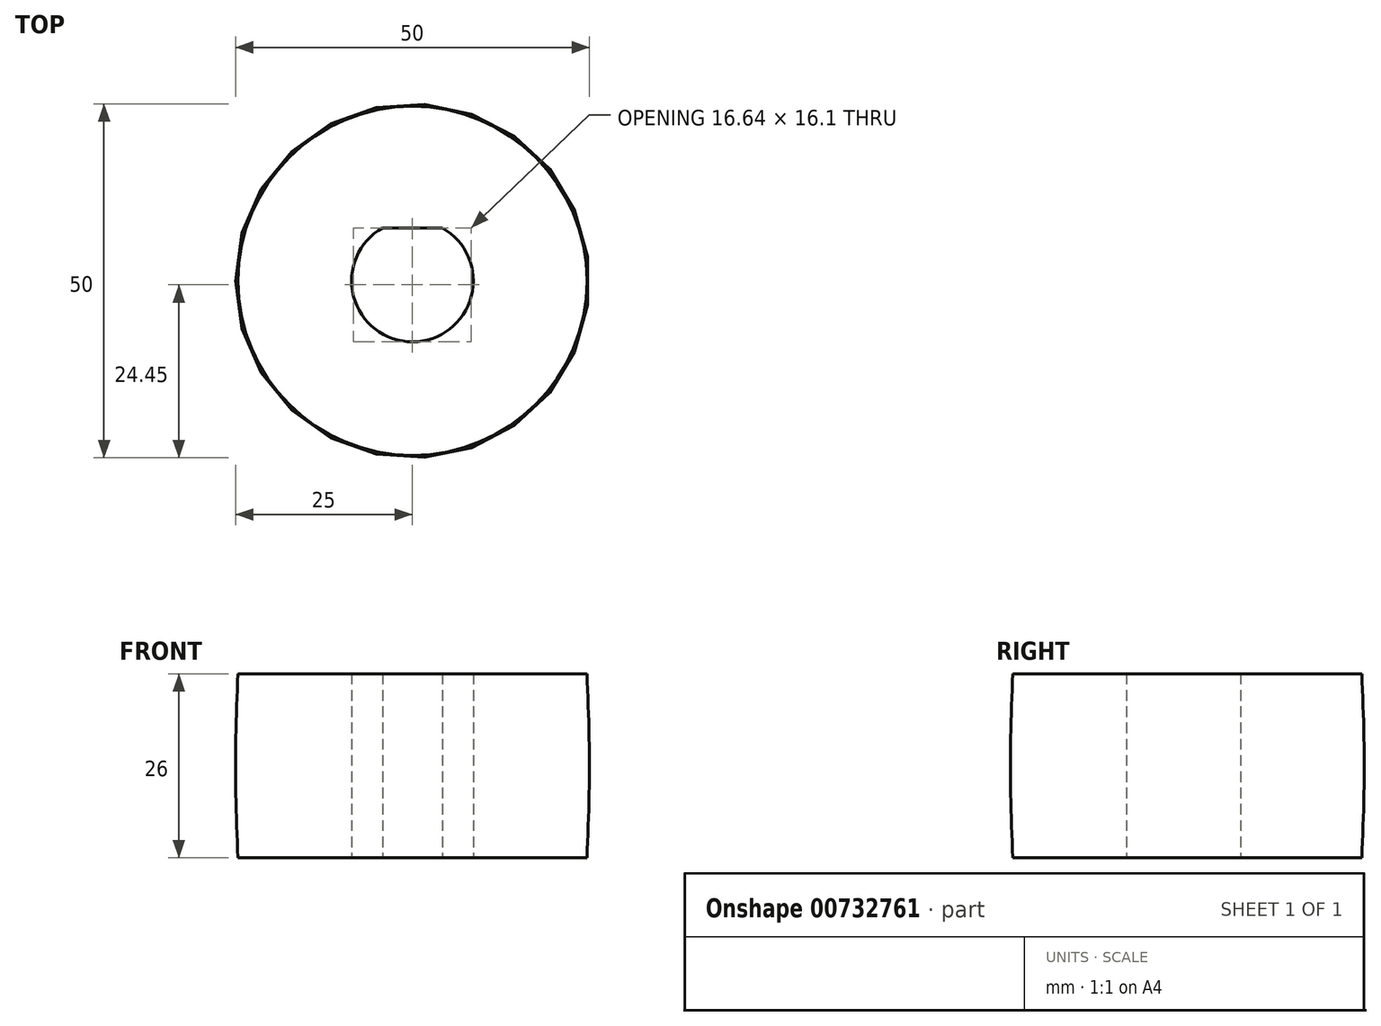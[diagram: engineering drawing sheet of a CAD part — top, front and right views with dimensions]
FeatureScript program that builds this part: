
annotation { "Feature Type Name" : "Feature", "Feature Type Description" : "" }
export const myFeature = defineFeature(function(context is Context, id is Id, definition is map)
    precondition{}
    {
        {
            var Q0;
            Q0=qCreatedBy(makeId("Top.planeOp"),FACE);
            var sketch = newSketch(context, id + "F0", { "sketchPlane" : qUnion([Q0])});
            skCircle(sketch, "E0", {"center": v(0, 0) * mm, "radius": 8.6 * mm});
            skCircle(sketch, "E1", {"center": v(0, 0) * mm, "radius": 25 * mm});
            skLineSegment(sketch, "E2", {"start": v(-4.2, 7.5) * mm, "end": v(4.2, 7.5) * mm});
            skSolve(sketch);
        }
        {
            var Q0;
            Q0=makeQuery(id+"F0.imprint","IMPRINT",FACE,{"disambiguationData":[TD([[makeQuery(id+"F0.imprint","IMPRINT",EDGE,{"derivedFrom":sQuery(id+"F0.wireOp",EDGE,"E0")}),-1.0]])]});
            var Q1;
            {var subQ0=sQuery(id+"F0.wireOp",EDGE,"E2");Q1=makeQuery(id+"F0.imprint","IMPRINT",FACE,{"disambiguationData":[TD([[makeQuery(id+"F0.imprint","IMPRINT",EDGE,{"derivedFrom":subQ0}),1.0]])]});}
            extrude(context, id + "F1", {"entities" : qUnion([Q0, Q1]), "endBound" : BoundingType.SYMMETRIC, "depth" : 26 * mm, "offsetDistance" : 25 * mm});
        }
        {
            var Q0;
            Q0=qCreatedBy(makeId("Front.planeOp"),FACE);
            var sketch = newSketch(context, id + "F2", { "sketchPlane" : qUnion([Q0])});
            skLineSegment(sketch, "E3.bottom", {"start": v(-24.66, 13) * mm, "end": v(-43.25, 13) * mm});
            skLineSegment(sketch, "E3.top", {"start": v(-24.66, -13) * mm, "end": v(-43.25, -13) * mm});
            skLineSegment(sketch, "E3.left", {"start": v(-24.66, 13) * mm, "end": v(-24.66, -13) * mm});
            skLineSegment(sketch, "E3.right", {"start": v(-43.25, 13) * mm, "end": v(-43.25, -13) * mm});
            skLineSegment(sketch, "E4", {"start": v(-24.66, 13) * mm, "end": v(-25, 0) * mm, "construction": true});
            skLineSegment(sketch, "E5", {"start": v(-24.66, -13) * mm, "end": v(-25, 0) * mm, "construction": true});
            skFitSpline(sketch, "E6", {"points": [v(-24.66, -13) * mm, v(-25, 0) * mm, v(-24.66, 13) * mm], "startDerivative": vector(-1.02, 26) * mm, "endDerivative": vector(1.02, 26) * mm});
            skLineSegment(sketch, "E7", {"start": v(0, 13.98) * mm, "end": v(0, -14.3) * mm});
            skSolve(sketch);
        }
        {
            var Q0;
            Q0=makeQuery(id+"F2.imprint","IMPRINT",FACE,{"disambiguationData":[TD([[makeQuery(id+"F2.imprint","IMPRINT",EDGE,{"derivedFrom":sQuery(id+"F2.wireOp",EDGE,"E3.bottom")}),1.0]])]});
            var Q1;
            Q1=sQuery(id+"F2.wireOp",EDGE,"E7");
            revolve(context, id + "F3", {"operationType" : NewBodyOperationType.REMOVE, "surfaceOperationType" : NewSurfaceOperationType.NEW, "entities" : qUnion([Q0]), "axis" : qUnion([Q1]), "revolveType" : RevolveType.FULL, "oppositeDirection" : true});
        }
    });
